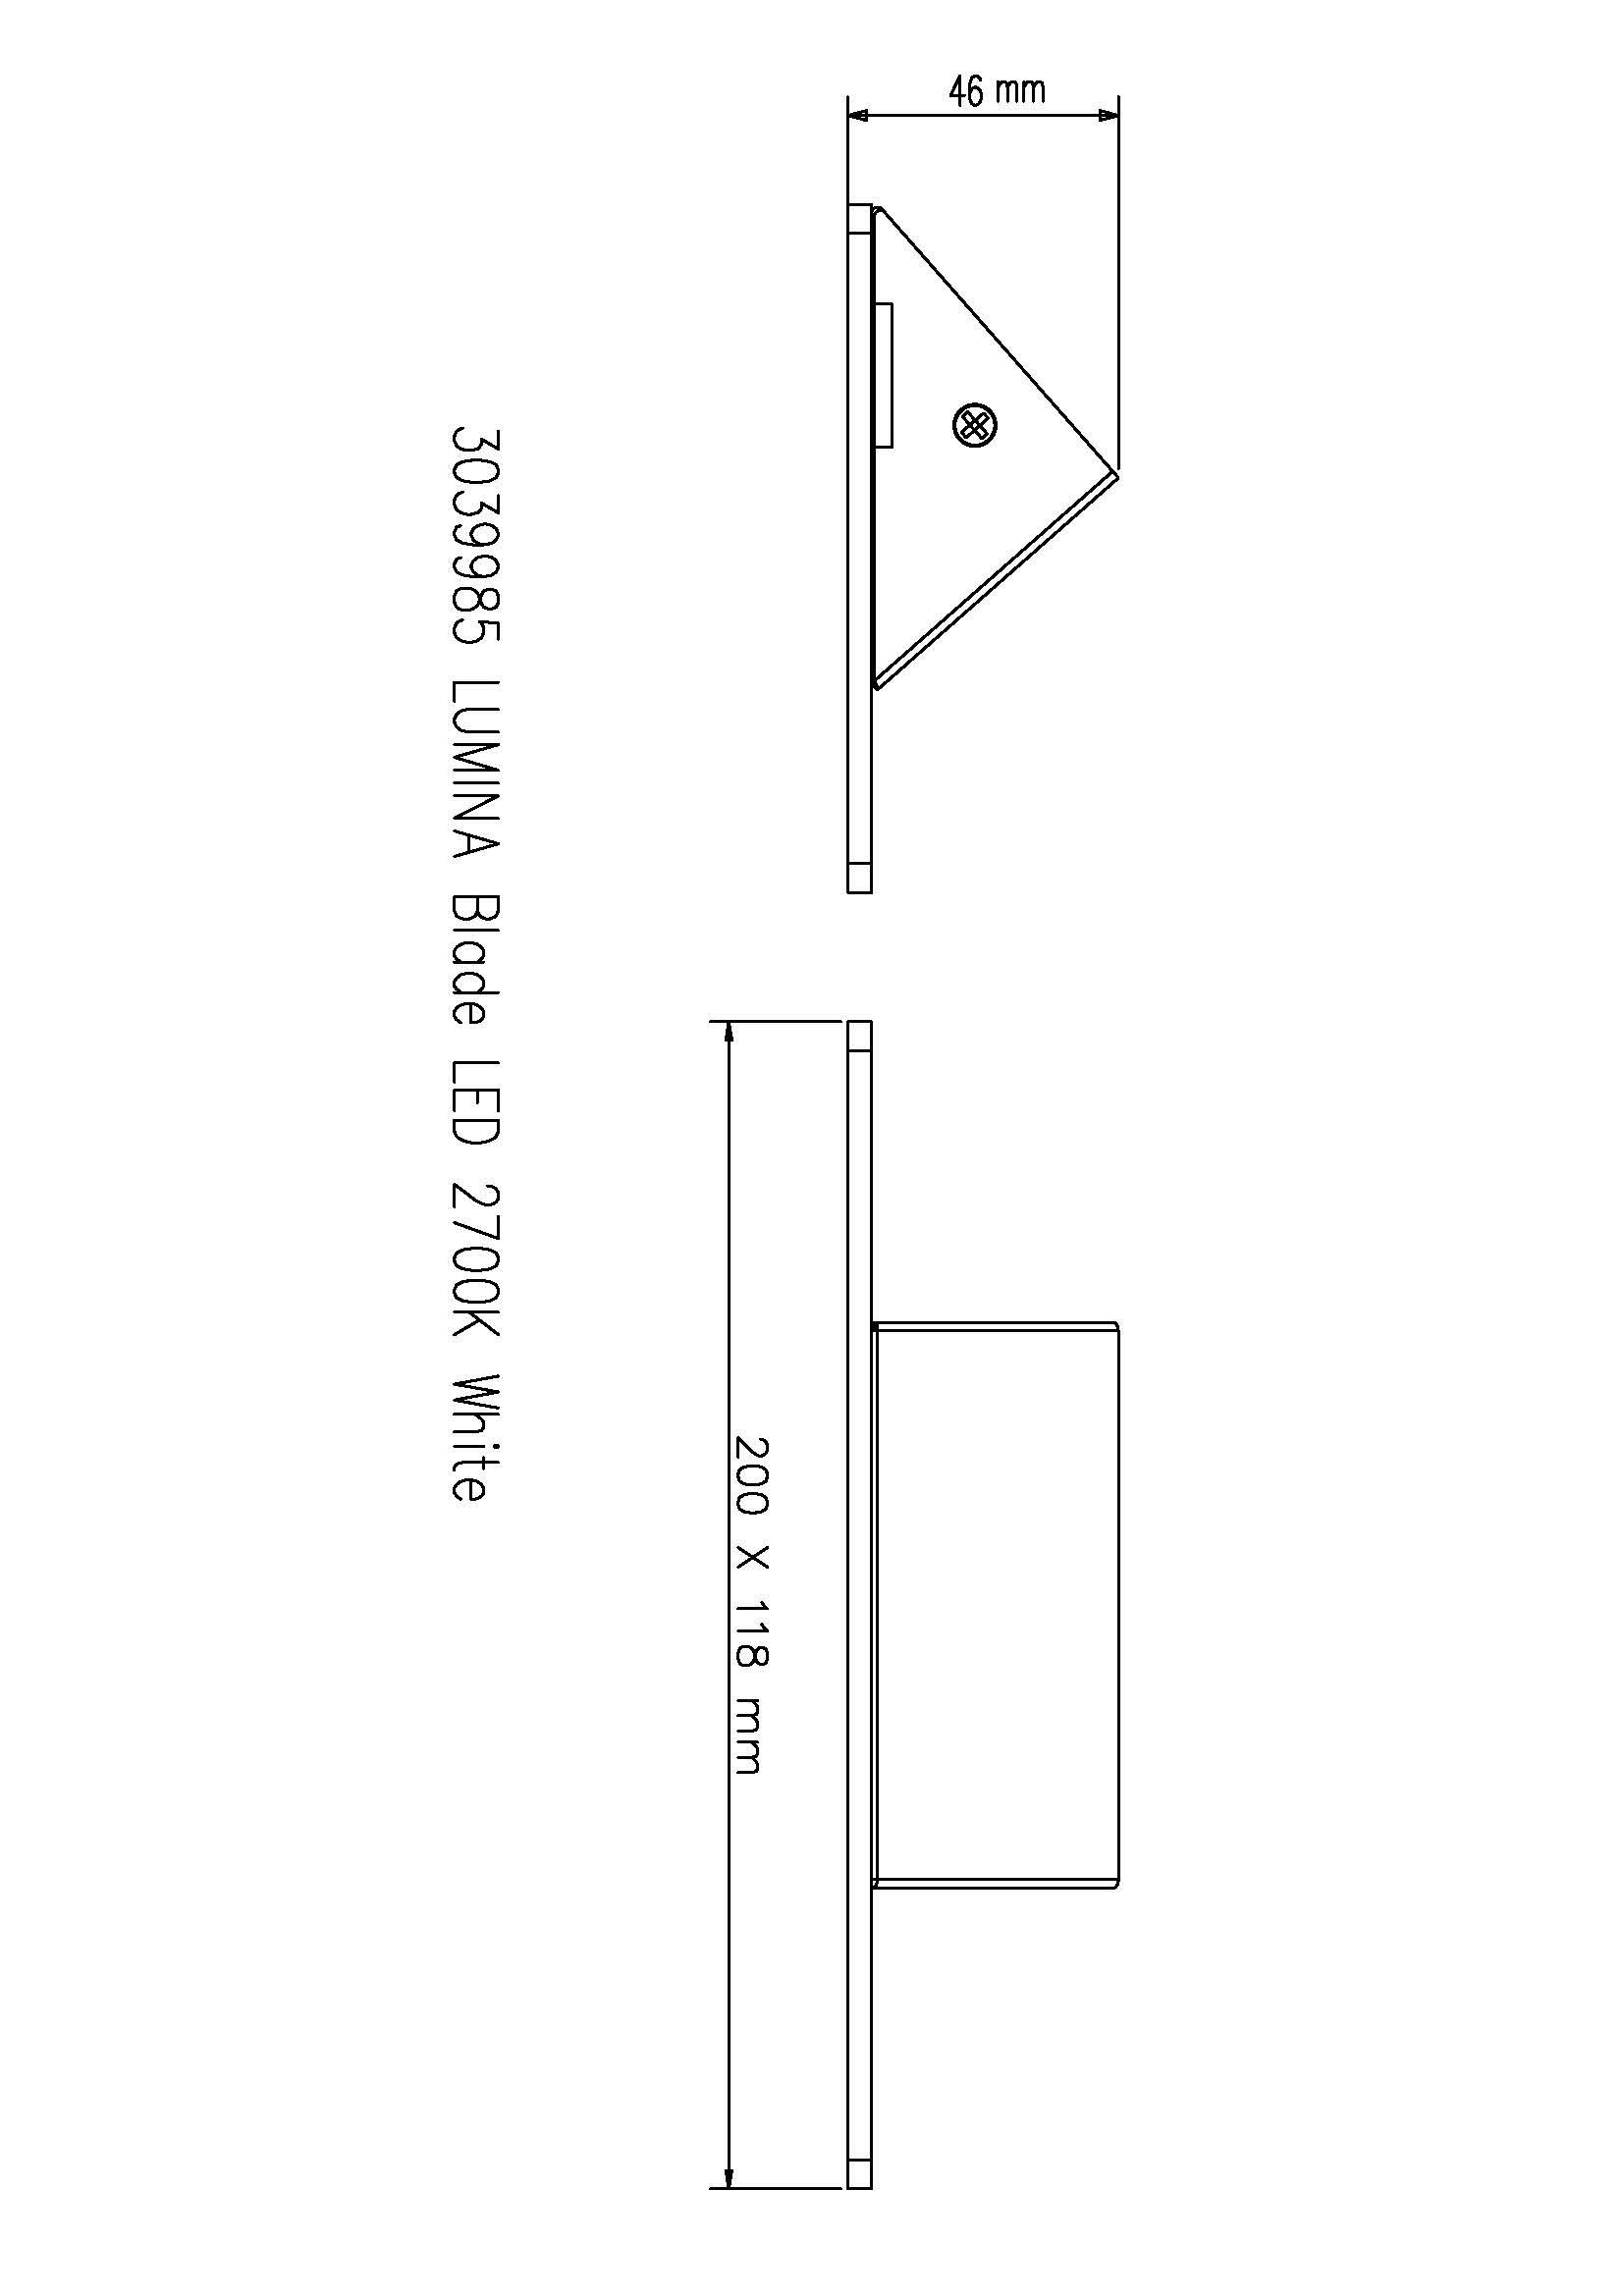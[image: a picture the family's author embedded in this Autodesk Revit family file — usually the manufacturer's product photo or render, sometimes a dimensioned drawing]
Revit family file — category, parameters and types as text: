
# Revit family: 3039982 Lighting Fixture_Sylvania_Lumina Cube LED_Wall Mounted
name_source: partatom
category: Lighting Fixtures
revit_build: Autodesk Revit 2017 (Build: 20190507_1515(x64)
units: mm (PartAtom-declared; Revit-internal decimal feet)

## family parameters
Cut with Voids When Loaded = No
Host = Face
Light Source = Yes
OmniClass Number = 23.80.70.11.17
OmniClass Title = Specialized Lighting by Location or Use
Part Type = Normal
Room Calculation Point = No
Round Connector Dimension = Use Diameter
Shared = No

## types (1)
- Lumina Cube LED 2700K
    Accessory Material = Aluminum_Sylvania_Cube LED_White_RAL 9016
    Apparent Load = 6 VA
    Assembly Code = D5020200
    Body Material = Aluminum_Sylvania_Cube LED_White_RAL 9016
    Color Filter = 16777215
    Default Elevation = 0 mm  [stored 0 ft]
    Description = Lumina LED is a new range of ambient & decorative LED wall lights. Consisting of multiple decorative styles, they are suitable for use in any hospitality or residential application such as reception areas, hallways and lounge spaces. Lumina LED offers a selection of different styles to suit multiple applications. With a 2,700K colour temperature it provides a soft and ambient lighting effect. Lumina LED provides direct/indirect ambient light with an efficacy of up to 87lm/W; up to 50% more energy efficient than equivalent products using traditional lamp sources.
    Dimming Lamp Color Temperature Shift = <None>
    Drive Current = 500mA
    Electrical Protection = Class II
    Emit Shape Visible in Rendering = No
    Emit from Circle Diameter = 7 mm  [stored 0.0229659 ft]
    Energy Class = A++, A+, A
    Height = 62 mm  [stored 0.203412 ft]
    IP Rating = IP20
    Lamp = LED
    Length = 100 mm  [stored 0.328084 ft]
    Life = 30 000h
    Light Distribution = Direct/Indirect
    Manufacturer = Feilo Sylvania
    Model = 3039982 Lumina Cube LED 2700K
    Photometric Web File = 3039982_LuminaCubeLED2700K-183012.ies
    Product Family = Lumina LED
    Product Page URL = http://www.sylvania-lighting.com
    Tilt Angle = 90.00°
    URL = http://www.sylvania-lighting.com
    Voltage = 240 V
    Voltage Comments = UNV (Universal Voltage; 100-240 Volt)
    Width = 100 mm  [stored 0.328084 ft]

note: [stored X ft] marks values corroborated as IEEE doubles in the binary element streams (Revit-internal decimal feet)

## geometry (parser evidence)
native form markers: Blend x2, Sweep x3
no freeform markers — native parametric forms only
